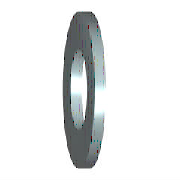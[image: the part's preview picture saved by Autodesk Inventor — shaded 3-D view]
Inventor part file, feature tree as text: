
AUTODESK INVENTOR PART (.ipt)
format: ipt  version: 2015 (Build 190159000, 159)  size: 108,032 bytes
history: native  units: mm (DEFAULTED — no unit token found)
features: extrude x1, other x1, plane x1, sketch x1
ambient origin geometry x7: Origin, YZ Plane, XY Plane, X Axis, Y Axis, Z Axis, Center Point
bodies: Solid1 (feature_tree)
feature tree (4):
  extrude  "Bryła"  Depth=5.3mm
  other  "Work Axis1"
  plane  "Work Plane1"
  sketch  "Szkic"
